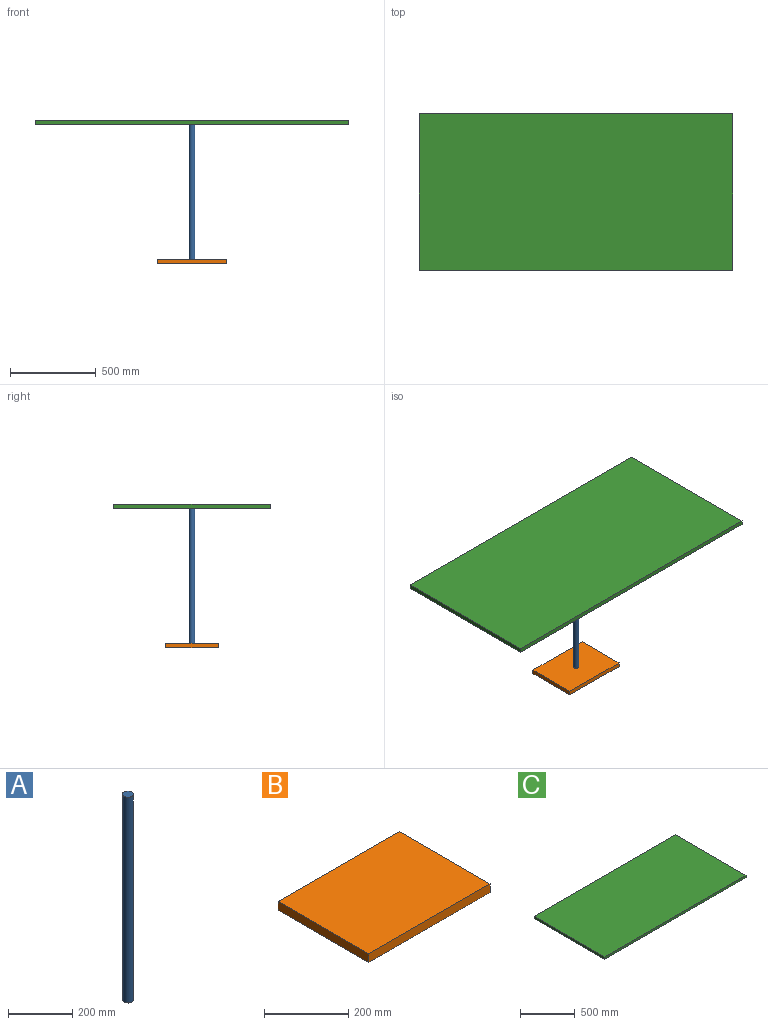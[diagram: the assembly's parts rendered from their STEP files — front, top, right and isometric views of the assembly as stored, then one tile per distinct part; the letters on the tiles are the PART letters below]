
ASSEMBLY  parts=3 mates=2
PART A: 3 faces, bbox 33.8x33.8x787.4 mm
  f0: cylinder r=16.89mm len=787.4mm, axis (0,0,-1), area 83579.1mm2, adj f1,f2
  f1: plane 33.79x33.79mm, normal (0,0,-1), area 896.6mm2, adj f0
  f2: plane 33.79x33.79mm, normal (0,0,1), area 896.6mm2, adj f0
PART B: 6 faces, bbox 406.4x304.8x25.4 mm
  f0: plane 406.4x25.4mm, normal (0,1,0), area 10322.6mm2, adj f1,f3,f4,f5
  f1: plane 304.8x25.4mm, normal (-1,0,0), area 7741.9mm2, adj f0,f2,f4,f5
  f2: plane 406.4x25.4mm, normal (0,-1,0), area 10322.6mm2, adj f1,f3,f4,f5
  f3: plane 304.8x25.4mm, normal (1,0,0), area 7741.9mm2, adj f0,f2,f4,f5
  f4: plane 406.4x304.8mm, normal (0,0,1), area 123870.7mm2, adj f0,f1,f2,f3
  f5: plane 406.4x304.8mm, normal (0,0,-1), area 123870.7mm2, adj f0,f1,f2,f3
PART C: 6 faces, bbox 1828.8x914.4x25.4 mm
  f0: plane 1828.8x25.4mm, normal (0,1,0), area 46451.5mm2, adj f1,f3,f4,f5
  f1: plane 914.4x25.4mm, normal (-1,0,0), area 23225.8mm2, adj f0,f2,f4,f5
  f2: plane 1828.8x25.4mm, normal (0,-1,0), area 46451.5mm2, adj f1,f3,f4,f5
  f3: plane 914.4x25.4mm, normal (1,0,0), area 23225.8mm2, adj f0,f2,f4,f5
  f4: plane 1828.8x914.4mm, normal (0,0,1), area 1672254.7mm2, adj f0,f1,f2,f3
  f5: plane 1828.8x914.4mm, normal (0,0,-1), area 1672254.7mm2, adj f0,f1,f2,f3
PLACE A rot(axis=(0,0,1),90deg) t=(286.71,-286.71,-360.31)mm
PLACE B t=(289.04,-297.78,-385.71)mm
PLACE C t=(282.92,20.16,427.09)mm
MATE planar A.f0 <-> B.f4  axis (0,0,-1) through (286.71,-286.71,-360.31)mm
MATE planar C.f5 <-> A.f0  axis (0,0,-1) through (286.71,-286.71,427.09)mm
